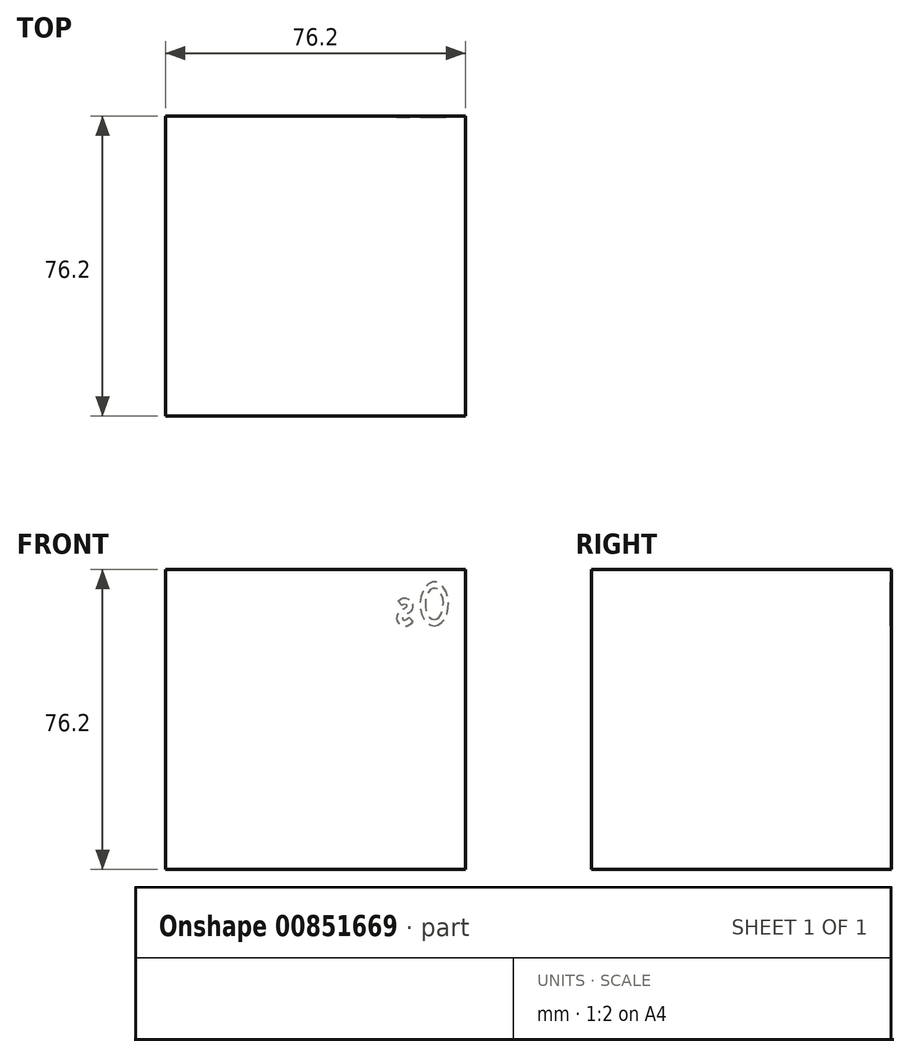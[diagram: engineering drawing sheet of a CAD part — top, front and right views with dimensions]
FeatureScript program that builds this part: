
annotation { "Feature Type Name" : "Feature", "Feature Type Description" : "" }
export const myFeature = defineFeature(function(context is Context, id is Id, definition is map)
    precondition{}
    {
        {
            var Q0;
            Q0=qCreatedBy(makeId("Front.planeOp"),FACE);
            var sketch = newSketch(context, id + "F0", { "sketchPlane" : qUnion([Q0])});
            skLineSegment(sketch, "E0.bottom", {"start": v(38.1, -38.1) * mm, "end": v(-38.1, -38.1) * mm});
            skLineSegment(sketch, "E0.top", {"start": v(38.1, 38.1) * mm, "end": v(-38.1, 38.1) * mm});
            skLineSegment(sketch, "E0.left", {"start": v(38.1, -38.1) * mm, "end": v(38.1, 38.1) * mm});
            skLineSegment(sketch, "E0.right", {"start": v(-38.1, -38.1) * mm, "end": v(-38.1, 38.1) * mm});
            skPoint(sketch, "E0.middle", {"position": v(0, 0) * mm});
            skSolve(sketch);
        }
        {
            var Q0;
            Q0=makeQuery(id+"F0.imprint","IMPRINT",FACE,{"disambiguationData":[TD([[makeQuery(id+"F0.imprint","IMPRINT",EDGE,{"derivedFrom":sQuery(id+"F0.wireOp",EDGE,"E0.bottom")}),-1.0]])]});
            extrude(context, id + "F1", {"entities" : qUnion([Q0]), "depth" : 76.2 * mm, "offsetDistance" : 25 * mm});
        }
        {
            var Q0;
            Q0=qCreatedBy(makeId("Front.planeOp"),FACE);
            var sketch = newSketch(context, id + "F2", { "sketchPlane" : qUnion([Q0])});
            skEllipse(sketch, "E1", {"center": v(30.17, 29.36) * mm, "majorRadius": 5.56 * mm, "minorRadius": 3.6 * mm, "majorAxis": v(0, -1)});
            skEllipse(sketch, "E2", {"center": v(30.17, 29.36) * mm, "majorRadius": 3.98 * mm, "minorRadius": 2.29 * mm, "majorAxis": v(0, -1)});
            skFitSpline(sketch, "E3", {"points": [v(21.5, 29.56) * mm, v(22, 29.95) * mm, v(22.73, 30.09) * mm, v(23.55, 29.74) * mm, v(23.91, 28.96) * mm, v(23.66, 28.07) * mm, v(23.09, 27.6) * mm, v(22.44, 27.24) * mm, v(21.78, 26.84) * mm, v(21.36, 26.07) * mm, v(21.48, 25.19) * mm, v(22.5, 24.49) * mm, v(23.58, 24.8) * mm, v(24.26, 25.43) * mm], "startDerivative": vector(10.56, 10.08) * mm, "endDerivative": vector(10.31, 10.99) * mm});
            skFitSpline(sketch, "E4.0", {"points": [v(20.98, 30.1) * mm, v(21.03, 30.16) * mm, v(21.14, 30.25) * mm, v(21.28, 30.38) * mm, v(21.45, 30.5) * mm, v(21.64, 30.61) * mm, v(21.84, 30.7) * mm, v(22.13, 30.79) * mm, v(22.46, 30.85) * mm, v(22.84, 30.84) * mm, v(23.22, 30.78) * mm, v(23.57, 30.64) * mm, v(23.9, 30.44) * mm, v(24.2, 30.18) * mm, v(24.48, 29.78) * mm, v(24.64, 29.3) * mm, v(24.67, 28.9) * mm, v(24.66, 28.61) * mm, v(24.6, 28.33) * mm, v(24.51, 28.06) * mm, v(24.4, 27.8) * mm, v(24.23, 27.56) * mm, v(24.04, 27.36) * mm, v(23.85, 27.2) * mm, v(23.67, 27.08) * mm, v(23.51, 26.98) * mm, v(23.37, 26.9) * mm, v(23.22, 26.81) * mm, v(23.07, 26.73) * mm, v(22.92, 26.64) * mm, v(22.75, 26.56) * mm, v(22.6, 26.48) * mm, v(22.48, 26.42) * mm, v(22.39, 26.36) * mm, v(22.32, 26.31) * mm, v(22.26, 26.26) * mm, v(22.17, 26.13) * mm, v(22.1, 25.98) * mm, v(22.08, 25.85) * mm, v(22.07, 25.75) * mm, v(22.09, 25.66) * mm, v(22.14, 25.54) * mm, v(22.28, 25.39) * mm, v(22.4, 25.3) * mm, v(22.5, 25.25) * mm, v(22.57, 25.23) * mm, v(22.61, 25.23) * mm, v(22.66, 25.23) * mm, v(22.73, 25.23) * mm, v(22.87, 25.26) * mm, v(23.04, 25.34) * mm, v(23.18, 25.42) * mm, v(23.27, 25.49) * mm, v(23.35, 25.56) * mm, v(23.47, 25.68) * mm, v(23.6, 25.82) * mm, v(23.71, 25.94) * mm]});
            skLineSegment(sketch, "E5.0", {"start": v(43.1, 43.1) * mm, "end": v(43.1, -43.1) * mm});
            skLineSegment(sketch, "E5.1", {"start": v(-43.1, 43.1) * mm, "end": v(43.1, 43.1) * mm});
            skLineSegment(sketch, "E5.2", {"start": v(-43.1, -43.1) * mm, "end": v(-43.1, 43.1) * mm});
            skLineSegment(sketch, "E5.3", {"start": v(43.1, -43.1) * mm, "end": v(-43.1, -43.1) * mm});
            skFitSpline(sketch, "E6.0", {"points": [v(22.01, 29.02) * mm, v(22.12, 29.12) * mm, v(22.23, 29.22) * mm, v(22.27, 29.24) * mm, v(22.29, 29.26) * mm, v(22.36, 29.29) * mm, v(22.47, 29.32) * mm, v(22.6, 29.34) * mm, v(22.7, 29.34) * mm, v(22.8, 29.32) * mm, v(22.91, 29.28) * mm, v(23, 29.23) * mm, v(23.06, 29.17) * mm, v(23.13, 29.08) * mm, v(23.16, 28.98) * mm, v(23.17, 28.89) * mm, v(23.16, 28.8) * mm, v(23.15, 28.7) * mm, v(23.12, 28.62) * mm, v(23.09, 28.56) * mm, v(23.06, 28.52) * mm, v(23.04, 28.5) * mm, v(23, 28.45) * mm, v(22.95, 28.4) * mm, v(22.86, 28.34) * mm, v(22.75, 28.27) * mm, v(22.6, 28.19) * mm, v(22.48, 28.11) * mm, v(22.35, 28.04) * mm, v(22.21, 27.97) * mm, v(22.09, 27.9) * mm, v(21.94, 27.83) * mm, v(21.76, 27.74) * mm, v(21.57, 27.62) * mm, v(21.37, 27.48) * mm, v(21.16, 27.28) * mm, v(21, 27.07) * mm, v(20.8, 26.77) * mm, v(20.67, 26.44) * mm, v(20.6, 26.09) * mm, v(20.56, 25.72) * mm, v(20.6, 25.32) * mm, v(20.76, 24.92) * mm, v(21, 24.55) * mm, v(21.29, 24.25) * mm, v(21.65, 24) * mm, v(21.95, 23.85) * mm, v(22.23, 23.77) * mm, v(22.47, 23.73) * mm, v(22.7, 23.72) * mm, v(22.99, 23.75) * mm, v(23.4, 23.85) * mm, v(23.82, 24.04) * mm, v(24.21, 24.31) * mm, v(24.52, 24.6) * mm, v(24.7, 24.8) * mm, v(24.8, 24.91) * mm]});
            skLineSegment(sketch, "E7", {"start": v(22.01, 29.02) * mm, "end": v(20.98, 30.1) * mm});
            skLineSegment(sketch, "E8", {"start": v(24.8, 24.91) * mm, "end": v(23.71, 25.94) * mm});
            skSolve(sketch);
        }
        {
            var Q0;
            Q0=makeQuery(id+"F2.imprint","IMPRINT",FACE,{"disambiguationData":[TD([[makeQuery(id+"F2.imprint","IMPRINT",EDGE,{"derivedFrom":sQuery(id+"F2.wireOp",EDGE,"E1")}),1.0]])]});
            var Q1;
            {var subQ0=sQuery(id+"F2.wireOp",EDGE,"E3");Q1=makeQuery(id+"F2.imprint","IMPRINT",FACE,{"disambiguationData":[TD([[makeQuery(id+"F2.imprint","IMPRINT",EDGE,{"derivedFrom":subQ0}),1.0]])]});}
            var Q2;
            {var subQ0=sQuery(id+"F2.wireOp",EDGE,"E3");Q2=makeQuery(id+"F2.imprint","IMPRINT",FACE,{"disambiguationData":[TD([[makeQuery(id+"F2.imprint","IMPRINT",EDGE,{"derivedFrom":subQ0}),-1.0]])]});}
            extrude(context, id + "F3", {"entities" : qUnion([Q0, Q1, Q2]), "operationType" : NewBodyOperationType.REMOVE, "depth" : .25 * mm, "offsetDistance" : 25 * mm});
        }
    });
